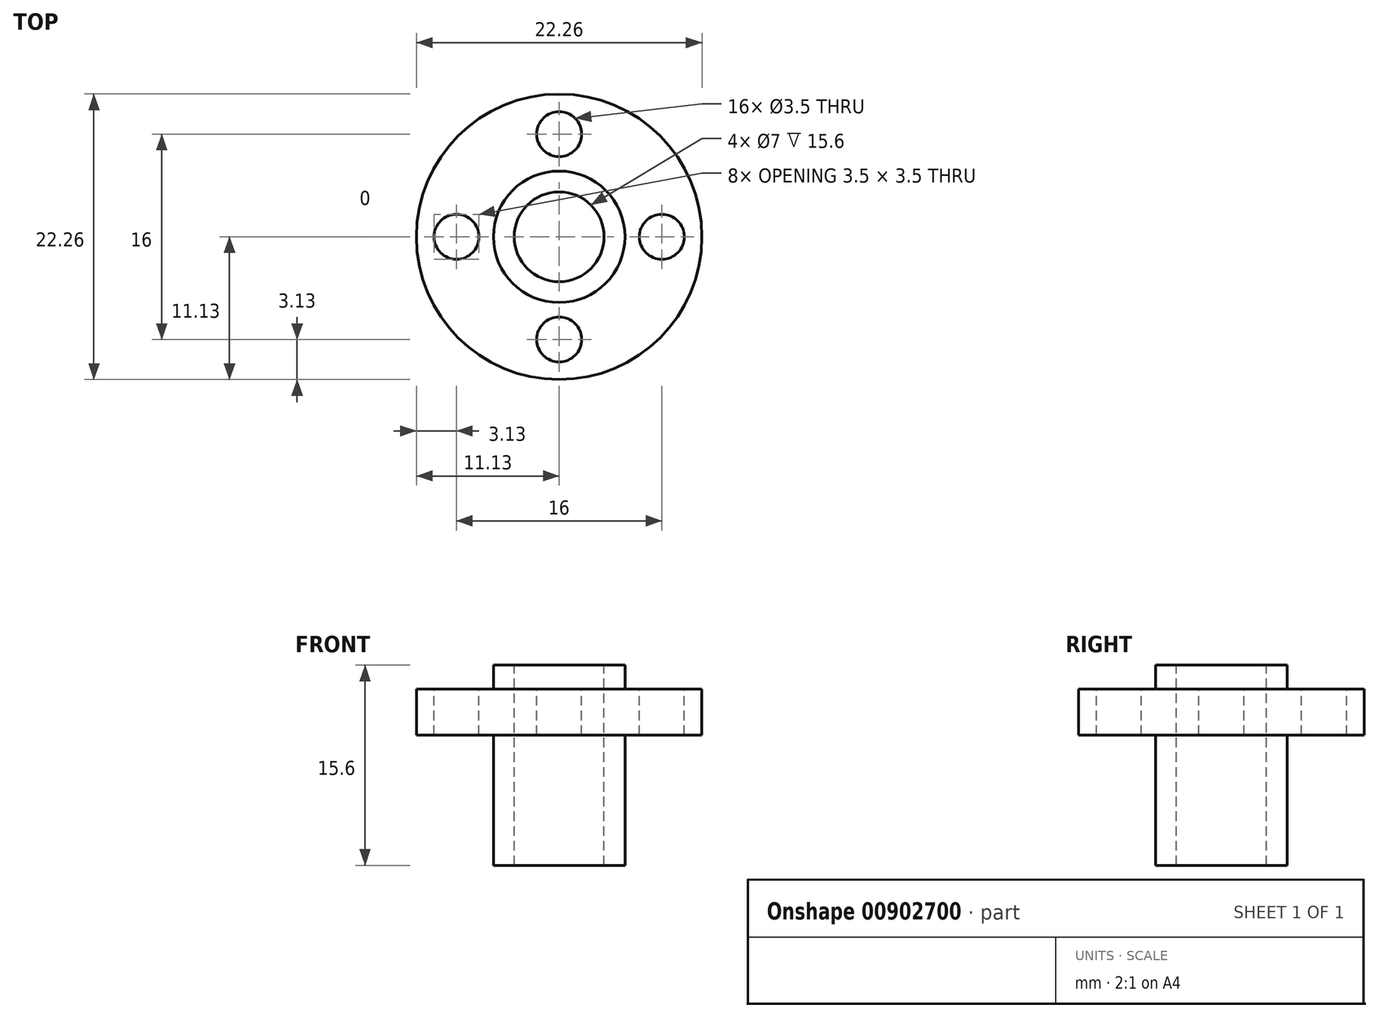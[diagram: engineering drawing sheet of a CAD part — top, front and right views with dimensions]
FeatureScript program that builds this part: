
annotation { "Feature Type Name" : "Feature", "Feature Type Description" : "" }
export const myFeature = defineFeature(function(context is Context, id is Id, definition is map)
    precondition{}
    {
        {
            var Q0;
            Q0=qCreatedBy(makeId("Front.planeOp"),FACE);
            var sketch = newSketch(context, id + "F0", { "sketchPlane" : qUnion([Q0])});
            skLineSegment(sketch, "E0", {"start": v(3.5, 1.85) * mm, "end": v(5.12, 1.85) * mm});
            skLineSegment(sketch, "E1", {"start": v(5.12, 1.85) * mm, "end": v(5.12, 0) * mm});
            skLineSegment(sketch, "E2", {"start": v(5.13, 0) * mm, "end": v(11.12, 0) * mm});
            skLineSegment(sketch, "E3", {"start": v(11.12, 0) * mm, "end": v(11.12, -3.6) * mm});
            skLineSegment(sketch, "E4", {"start": v(11.12, -3.6) * mm, "end": v(5.12, -3.6) * mm});
            skLineSegment(sketch, "E5", {"start": v(5.12, -3.6) * mm, "end": v(5.12, -13.75) * mm});
            skLineSegment(sketch, "E6", {"start": v(5.12, -13.75) * mm, "end": v(3.5, -13.75) * mm});
            skLineSegment(sketch, "E7", {"start": v(3.5, -13.75) * mm, "end": v(3.5, 1.85) * mm});
            skLineSegment(sketch, "E8", {"start": v(0, 0) * mm, "end": v(0, -24.26) * mm, "construction": true});
            skSolve(sketch);
        }
        {
            var Q0;
            Q0 = qSketchRegion(id + "F0", true);
            var Q1;
            Q1=sQuery(id+"F0.wireOp",EDGE,"E8");
            revolve(context, id + "F1", {"surfaceOperationType" : NewSurfaceOperationType.NEW, "entities" : qUnion([Q0]), "axis" : qUnion([Q1]), "revolveType" : RevolveType.FULL});
        }
        {
            var Q0;
            Q0=makeQuery(id+"F1.opRevolve","SWEPT_FACE",FACE,{"disambiguationData":[OSD([sQuery(id+"F0.wireOp",EDGE,"E2")])]});
            var sketch = newSketch(context, id + "F2", { "sketchPlane" : qUnion([Q0])});
            skCircle(sketch, "E9", {"center": v(0, 8) * mm, "radius": 1.75 * mm});
            skLineSegment(sketch, "E10", {"start": v(0, 0) * mm, "end": v(0, 8) * mm, "construction": true});
            skCircle(sketch, "E11.1.0", {"center": v(-8, 0) * mm, "radius": 1.75 * mm});
            skCircle(sketch, "E11.2.0", {"center": v(0, -8) * mm, "radius": 1.75 * mm});
            skCircle(sketch, "E11.3.0", {"center": v(8, 0) * mm, "radius": 1.75 * mm});
            skPoint(sketch, "E11.center", {"position": v(0, 0) * mm});
            skSolve(sketch);
        }
        {
            var Q0;
            Q0 = qSketchRegion(id + "F2", true);
            extrude(context, id + "F3", {"entities" : qUnion([Q0]), "operationType" : NewBodyOperationType.REMOVE, "oppositeDirection" : true, "depth" : 25 * mm, "offsetDistance" : 25 * mm});
        }
    });
